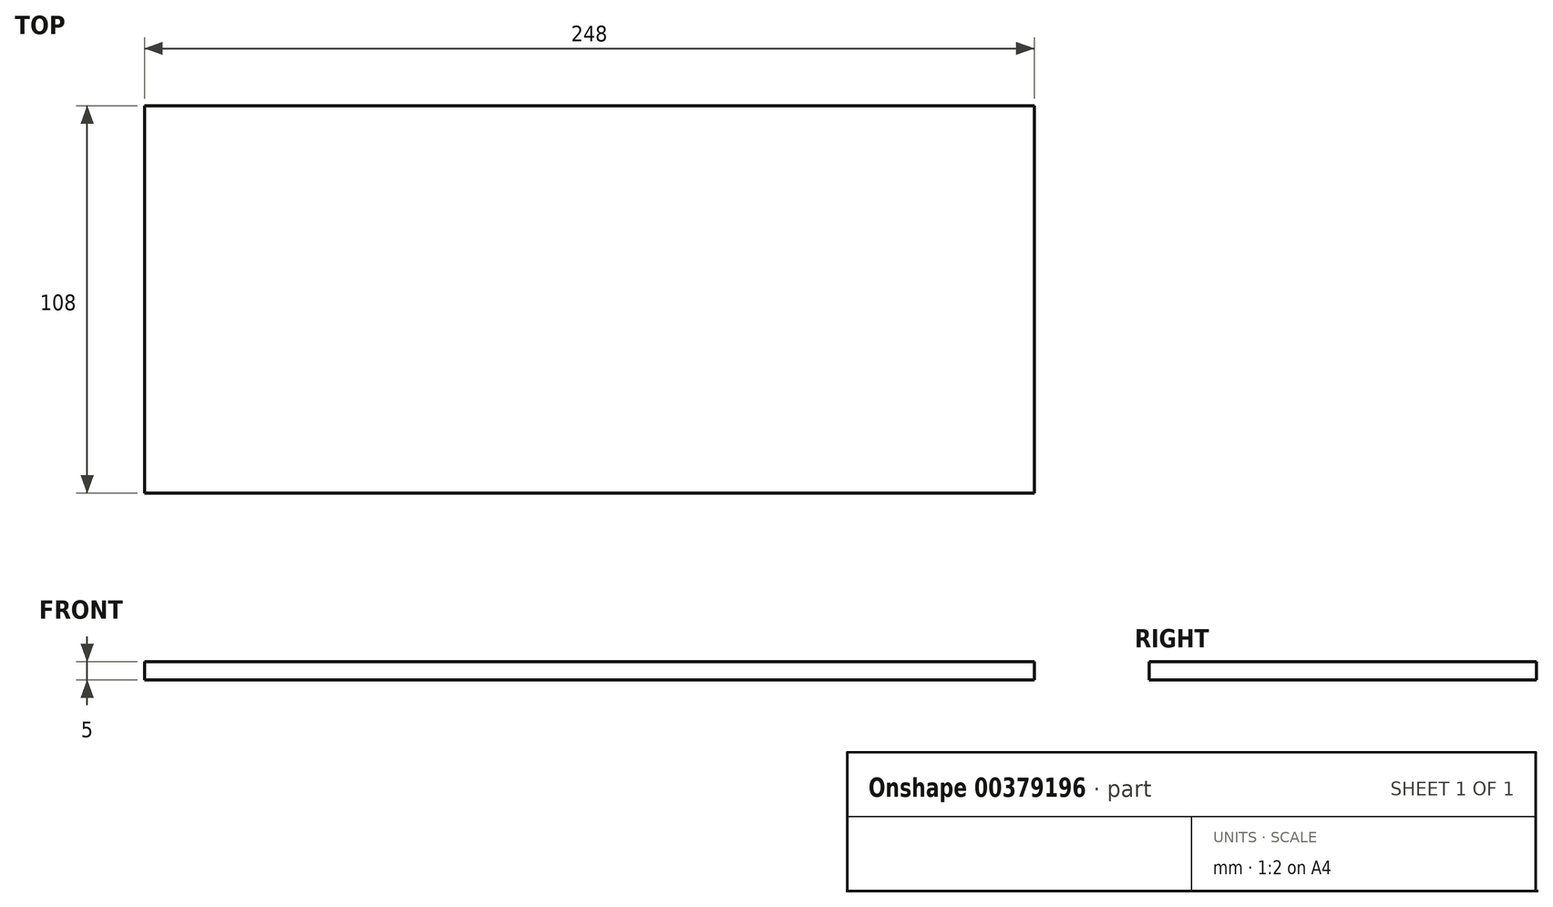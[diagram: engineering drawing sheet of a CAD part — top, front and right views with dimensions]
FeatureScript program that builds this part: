
annotation { "Feature Type Name" : "Feature", "Feature Type Description" : "" }
export const myFeature = defineFeature(function(context is Context, id is Id, definition is map)
    precondition{}
    {
        {
            var Q0;
            Q0=qCreatedBy(makeId("Top.planeOp"),FACE);
            var sketch = newSketch(context, id + "F0", { "sketchPlane" : qUnion([Q0])});
            skLineSegment(sketch, "E0.bottom", {"start": v(-124, 54) * mm, "end": v(124, 54) * mm});
            skLineSegment(sketch, "E0.top", {"start": v(-124, -54) * mm, "end": v(124, -54) * mm});
            skLineSegment(sketch, "E0.left", {"start": v(-124, 54) * mm, "end": v(-124, -54) * mm});
            skLineSegment(sketch, "E0.right", {"start": v(124, 54) * mm, "end": v(124, -54) * mm});
            skSolve(sketch);
        }
        {
            var Q0;
            Q0=makeQuery(id+"F0.imprint","IMPRINT",FACE,{"disambiguationData":[TD([[makeQuery(id+"F0.imprint","IMPRINT",EDGE,{"derivedFrom":sQuery(id+"F0.wireOp",EDGE,"E0.bottom")}),-1.0]])]});
            extrude(context, id + "F1", {"entities" : qUnion([Q0]), "depth" : 5 * mm});
        }
    });
